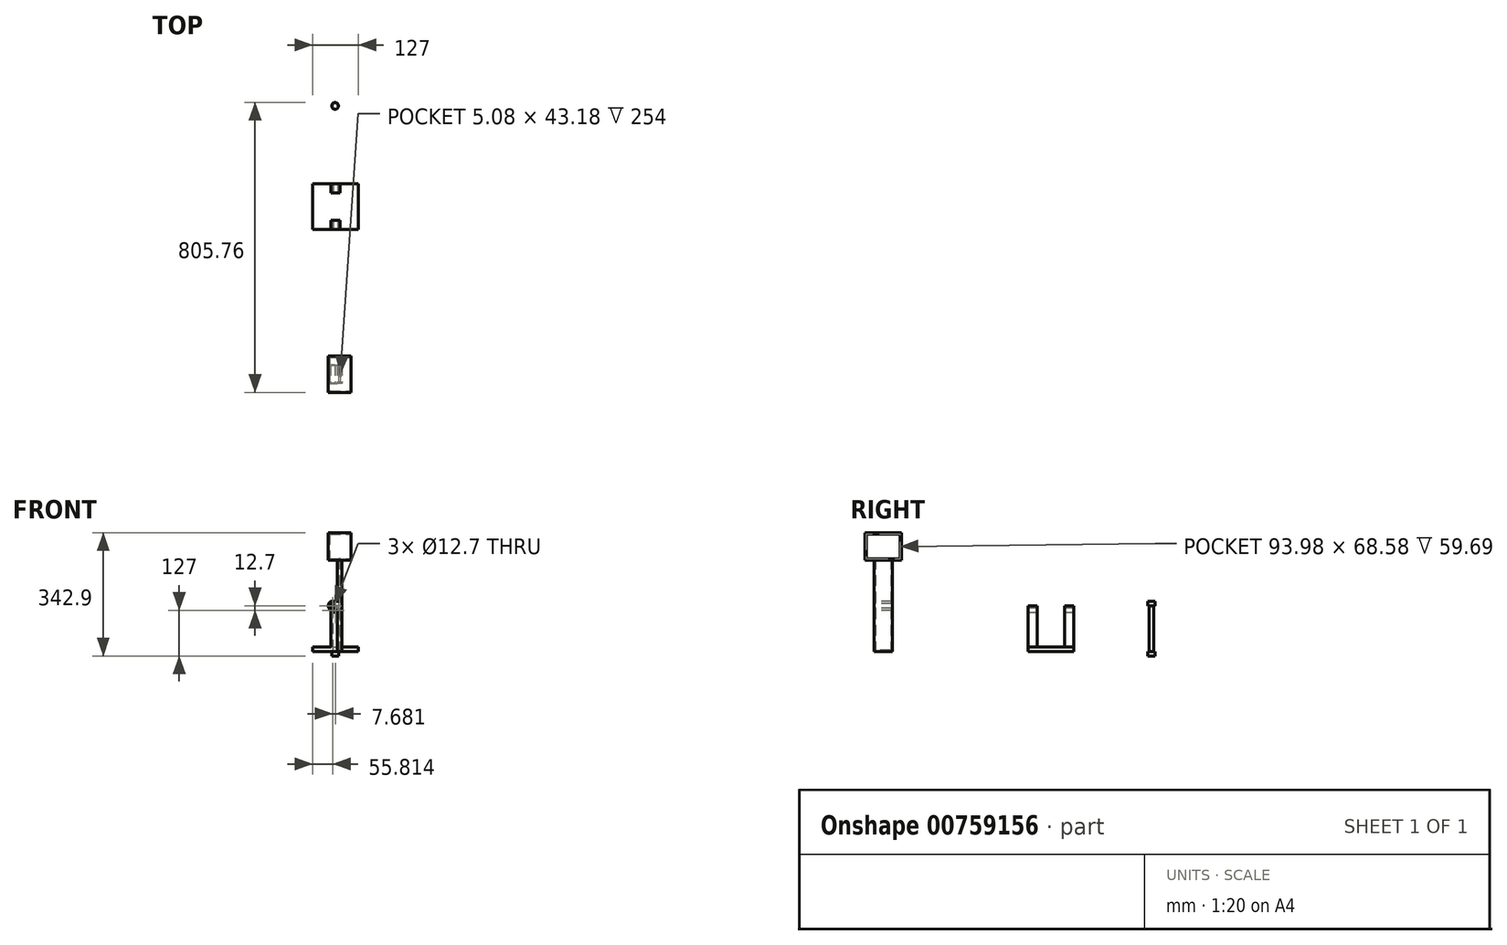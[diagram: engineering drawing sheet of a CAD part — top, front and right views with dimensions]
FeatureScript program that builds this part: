
annotation { "Feature Type Name" : "Feature", "Feature Type Description" : "" }
export const myFeature = defineFeature(function(context is Context, id is Id, definition is map)
    precondition{}
    {
        {
            var Q0;
            Q0=qCreatedBy(makeId("Top.planeOp"),FACE);
            var sketch = newSketch(context, id + "F0", { "sketchPlane" : qUnion([Q0])});
            skLineSegment(sketch, "E0.bottom", {"start": v(-62.3, 72.06) * mm, "end": v(64.7, 72.06) * mm});
            skLineSegment(sketch, "E0.top", {"start": v(-62.3, -54.94) * mm, "end": v(64.7, -54.94) * mm});
            skLineSegment(sketch, "E0.left", {"start": v(-62.3, 72.06) * mm, "end": v(-62.3, -54.94) * mm});
            skLineSegment(sketch, "E0.right", {"start": v(64.7, 72.06) * mm, "end": v(64.7, -54.94) * mm});
            skCircle(sketch, "E1", {"center": v(0, 288.32) * mm, "radius": 6.35 * mm});
            skLineSegment(sketch, "E2.bottom", {"start": v(18.92, -431.71) * mm, "end": v(6.22, -431.71) * mm});
            skLineSegment(sketch, "E2.top", {"start": v(18.92, -482.51) * mm, "end": v(6.22, -482.51) * mm});
            skLineSegment(sketch, "E2.left", {"start": v(18.92, -431.71) * mm, "end": v(18.92, -482.51) * mm});
            skLineSegment(sketch, "E2.right", {"start": v(6.22, -431.71) * mm, "end": v(6.22, -482.51) * mm});
            skPoint(sketch, "E2.middle", {"position": v(12.57, -457.11) * mm});
            skSolve(sketch);
        }
        {
            var Q0;
            Q0=makeQuery(id+"F0.imprint","IMPRINT",FACE,{"disambiguationData":[TD([[makeQuery(id+"F0.imprint","IMPRINT",EDGE,{"derivedFrom":sQuery(id+"F0.wireOp",EDGE,"E0.bottom")}),-1.0]])]});
            extrude(context, id + "F1", {"entities" : qUnion([Q0]), "depth" : 12.7 * mm, "offsetDistance" : 25.4 * mm});
        }
        {
            var Q0;
            Q0=makeQuery(id+"F1.opExtrude","CAP_FACE",FACE,{"disambiguationData":[OSD([sQuery(id+"F0.wireOp",EDGE,"E0.bottom"),sQuery(id+"F0.wireOp",EDGE,"E0.top"),sQuery(id+"F0.wireOp",EDGE,"E0.left"),sQuery(id+"F0.wireOp",EDGE,"E0.right")])],"isStart":false});
            var sketch = newSketch(context, id + "F2", { "sketchPlane" : qUnion([Q0])});
            skPoint(sketch, "E3.firstSnap0", {"position": v(1.2, 72.06) * mm});
            skLineSegment(sketch, "E4.bottom", {"start": v(13.9, -54.94) * mm, "end": v(-11.5, -54.94) * mm});
            skLineSegment(sketch, "E4.top", {"start": v(13.9, -29.54) * mm, "end": v(-11.5, -29.54) * mm});
            skLineSegment(sketch, "E4.left", {"start": v(13.9, -54.94) * mm, "end": v(13.9, -29.54) * mm});
            skLineSegment(sketch, "E4.right", {"start": v(-11.5, -54.94) * mm, "end": v(-11.5, -29.54) * mm});
            skPoint(sketch, "E4.middle", {"position": v(1.2, -42.24) * mm});
            skLineSegment(sketch, "E5.bottom", {"start": v(-11.5, 72.06) * mm, "end": v(13.9, 72.06) * mm});
            skLineSegment(sketch, "E5.top", {"start": v(-11.5, 46.66) * mm, "end": v(13.9, 46.66) * mm});
            skLineSegment(sketch, "E5.left", {"start": v(-11.5, 72.06) * mm, "end": v(-11.5, 46.66) * mm});
            skLineSegment(sketch, "E5.right", {"start": v(13.9, 72.06) * mm, "end": v(13.9, 46.66) * mm});
            skPoint(sketch, "E5.middle", {"position": v(1.2, 59.36) * mm});
            skPoint(sketch, "E5.middle.positionSnap0", {"position": v(1.2, -29.54) * mm});
            skPoint(sketch, "E5.centerSnap0", {"position": v(1.2, -29.54) * mm});
            skSolve(sketch);
        }
        {
            var Q0;
            Q0 = qSketchRegion(id + "F2", true);
            extrude(context, id + "F3", {"entities" : qUnion([Q0]), "operationType" : NewBodyOperationType.ADD, "depth" : 114.3 * mm, "offsetDistance" : 25.4 * mm});
        }
        {
            var Q0;
            Q0=makeQuery(id+"F3.opExtrude","CAP_EDGE",EDGE,{"disambiguationData":[OSD([sQuery(id+"F2.wireOp",EDGE,"E4.left")])],"isStart":false});
            fillet(context, id + "F4", {"entities" : qUnion([Q0]), "radius" : 12.7 * mm, "tangentPropagation" : true, "allowEdgeOverflow" : false});
        }
        {
            var Q0;
            Q0=makeQuery(id+"F3.opExtrude","CAP_EDGE",EDGE,{"disambiguationData":[OSD([sQuery(id+"F2.wireOp",EDGE,"E4.right")])],"isStart":false});
            fillet(context, id + "F5", {"entities" : qUnion([Q0]), "radius" : 12.7 * mm, "tangentPropagation" : true, "allowEdgeOverflow" : false});
        }
        {
            var Q0;
            Q0=makeQuery(id+"F3.opExtrude","CAP_EDGE",EDGE,{"disambiguationData":[OSD([sQuery(id+"F2.wireOp",EDGE,"E5.left")])],"isStart":false});
            var Q1;
            Q1=makeQuery(id+"F3.opExtrude","CAP_EDGE",EDGE,{"disambiguationData":[OSD([sQuery(id+"F2.wireOp",EDGE,"E5.right")])],"isStart":false});
            fillet(context, id + "F6", {"entities" : qUnion([Q0, Q1]), "radius" : 12.7 * mm, "tangentPropagation" : true, "allowEdgeOverflow" : false});
        }
        {
            var Q0;
            Q0=makeQuery(id+"F3.boolean.opBoolean","MERGE",FACE,{"derivedFrom":[makeQuery(id+"F1.opExtrude","SWEPT_FACE",FACE,{"disambiguationData":[OSD([sQuery(id+"F0.wireOp",EDGE,"E0.top")])]}),makeQuery(id+"F3.opExtrude","SWEPT_FACE",FACE,{"disambiguationData":[OSD([sQuery(id+"F2.wireOp",EDGE,"E4.bottom")])]})]});
            var sketch = newSketch(context, id + "F7", { "sketchPlane" : qUnion([Q0])});
            skCircle(sketch, "E6", {"center": v(1.2, 114.3) * mm, "radius": 6.35 * mm});
            skSolve(sketch);
        }
        {
            var Q0;
            Q0=makeQuery(id+"F7.imprint","IMPRINT",FACE,{"disambiguationData":[TD([[makeQuery(id+"F7.imprint","IMPRINT",EDGE,{"derivedFrom":sQuery(id+"F7.wireOp",EDGE,"E6")}),1.0]])]});
            extrude(context, id + "F8", {"entities" : qUnion([Q0]), "operationType" : NewBodyOperationType.REMOVE, "oppositeDirection" : true, "depth" : 153.42 * mm, "offsetDistance" : 25.4 * mm});
        }
        {
            var Q0;
            Q0=makeQuery(id+"F0.imprint","IMPRINT",FACE,{"disambiguationData":[TD([[makeQuery(id+"F0.imprint","IMPRINT",EDGE,{"derivedFrom":sQuery(id+"F0.wireOp",EDGE,"E1")}),1.0]])]});
            extrude(context, id + "F9", {"entities" : qUnion([Q0]), "depth" : 127 * mm, "offsetDistance" : 25.4 * mm});
        }
        {
            var Q0;
            Q0=makeQuery(id+"F9.opExtrude","CAP_FACE",FACE,{"disambiguationData":[OSD([sQuery(id+"F0.wireOp",EDGE,"E1")])],"isStart":false});
            var sketch = newSketch(context, id + "F10", { "sketchPlane" : qUnion([Q0])});
            skCircle(sketch, "E7", {"center": v(0, 288.32) * mm, "radius": 9.53 * mm});
            skSolve(sketch);
        }
        {
            var Q0;
            Q0 = qSketchRegion(id + "F10", true);
            extrude(context, id + "F11", {"entities" : qUnion([Q0]), "operationType" : NewBodyOperationType.ADD, "depth" : 12.7 * mm, "offsetDistance" : 25.4 * mm});
        }
        {
            var Q0;
            Q0=makeQuery(id+"F9.opExtrude","CAP_FACE",FACE,{"disambiguationData":[OSD([sQuery(id+"F0.wireOp",EDGE,"E1")])],"isStart":true});
            var sketch = newSketch(context, id + "F12", { "sketchPlane" : qUnion([Q0])});
            skCircle(sketch, "E8", {"center": v(0, -288.32) * mm, "radius": 9.53 * mm});
            skSolve(sketch);
        }
        {
            var Q0;
            Q0 = qSketchRegion(id + "F12", true);
            extrude(context, id + "F13", {"entities" : qUnion([Q0]), "operationType" : NewBodyOperationType.ADD, "depth" : 12.7 * mm, "offsetDistance" : 25.4 * mm});
        }
        {
            var Q0;
            Q0=makeQuery(id+"F0.imprint","IMPRINT",FACE,{"disambiguationData":[TD([[makeQuery(id+"F0.imprint","IMPRINT",EDGE,{"derivedFrom":sQuery(id+"F0.wireOp",EDGE,"E2.bottom")}),1.0]])]});
            extrude(context, id + "F14", {"entities" : qUnion([Q0]), "depth" : 254 * mm, "offsetDistance" : 25.4 * mm});
        }
        {
            var Q0;
            Q0=makeQuery(id+"F14.opExtrude","CAP_FACE",FACE,{"disambiguationData":[OSD([sQuery(id+"F0.wireOp",EDGE,"E2.bottom"),sQuery(id+"F0.wireOp",EDGE,"E2.top"),sQuery(id+"F0.wireOp",EDGE,"E2.left"),sQuery(id+"F0.wireOp",EDGE,"E2.right")])],"isStart":false});
            var sketch = newSketch(context, id + "F15", { "sketchPlane" : qUnion([Q0])});
            skLineSegment(sketch, "E9.bottom", {"start": v(-19.18, -406.31) * mm, "end": v(44.32, -406.31) * mm});
            skLineSegment(sketch, "E9.top", {"start": v(-19.18, -507.91) * mm, "end": v(44.32, -507.91) * mm});
            skLineSegment(sketch, "E9.left", {"start": v(-19.18, -406.31) * mm, "end": v(-19.18, -507.91) * mm});
            skLineSegment(sketch, "E9.right", {"start": v(44.32, -406.31) * mm, "end": v(44.32, -507.91) * mm});
            skPoint(sketch, "E9.middle", {"position": v(12.57, -457.11) * mm});
            skPoint(sketch, "E9.middle.positionSnap0", {"position": v(12.57, -431.71) * mm});
            skPoint(sketch, "E9.middle.positionSnap1", {"position": v(6.22, -457.11) * mm});
            skPoint(sketch, "E9.centerSnap0", {"position": v(12.57, -431.71) * mm});
            skPoint(sketch, "E9.centerSnap1", {"position": v(6.22, -457.11) * mm});
            skSolve(sketch);
        }
        {
            var Q0;
            Q0=makeQuery(id+"F15.imprint","IMPRINT",FACE,{"disambiguationData":[TD([[makeQuery(id+"F15.imprint","IMPRINT",EDGE,{"derivedFrom":makeQuery(id+"F14.opExtrude","CAP_EDGE",EDGE,{"disambiguationData":[OSD([sQuery(id+"F0.wireOp",EDGE,"E2.bottom")])],"isStart":false})}),1.0]])]});
            var Q1;
            Q1=makeQuery(id+"F15.imprint","IMPRINT",FACE,{"disambiguationData":[TD([[makeQuery(id+"F15.imprint","IMPRINT",EDGE,{"derivedFrom":sQuery(id+"F15.wireOp",EDGE,"E9.bottom")}),-1.0]])]});
            extrude(context, id + "F16", {"entities" : qUnion([Q0, Q1]), "operationType" : NewBodyOperationType.ADD, "depth" : 76.2 * mm, "offsetDistance" : 25.4 * mm});
        }
        {
            var Q0;
            Q0=makeQuery(id+"F16.opExtrude","SWEPT_FACE",FACE,{"disambiguationData":[OSD([sQuery(id+"F15.wireOp",EDGE,"E9.right")])]});
            shell(context, id + "F17", {"entities" : qUnion([Q0]), "thickness" : 3.8 * mm});
        }
        {
            var Q0;
            Q0=makeQuery(id+"F14.opExtrude","SWEPT_FACE",FACE,{"disambiguationData":[OSD([sQuery(id+"F0.wireOp",EDGE,"E2.right")])]});
            var sketch = newSketch(context, id + "F18", { "sketchPlane" : qUnion([Q0])});
            skPoint(sketch, "E10.middle", {"position": v(457.11, 127) * mm});
            skPoint(sketch, "E10.middle.positionSnap0", {"position": v(457.11, 0) * mm});
            skPoint(sketch, "E10.middle.positionSnap1", {"position": v(431.71, 127) * mm});
            skPoint(sketch, "E10.centerSnap0", {"position": v(457.11, 0) * mm});
            skPoint(sketch, "E10.centerSnap1", {"position": v(431.71, 127) * mm});
            skLineSegment(sketch, "E11.bottom", {"start": v(431.71, 139.7) * mm, "end": v(482.51, 139.7) * mm});
            skLineSegment(sketch, "E11.top", {"start": v(431.71, 114.3) * mm, "end": v(482.51, 114.3) * mm});
            skLineSegment(sketch, "E11.left", {"start": v(431.71, 139.7) * mm, "end": v(431.71, 114.3) * mm});
            skLineSegment(sketch, "E11.right", {"start": v(482.51, 139.7) * mm, "end": v(482.51, 114.3) * mm});
            skSolve(sketch);
        }
        {
            var Q0;
            Q0=makeQuery(id+"F18.imprint","IMPRINT",FACE,{"disambiguationData":[TD([[makeQuery(id+"F18.imprint","IMPRINT",EDGE,{"derivedFrom":sQuery(id+"F18.wireOp",EDGE,"E11.bottom")}),-1.0]])]});
            extrude(context, id + "F19", {"entities" : qUnion([Q0]), "operationType" : NewBodyOperationType.ADD, "depth" : 25.4 * mm, "offsetDistance" : 25.4 * mm});
        }
        {
            var Q0;
            Q0=makeQuery(id+"F19.opExtrude","CAP_EDGE",EDGE,{"disambiguationData":[OSD([sQuery(id+"F18.wireOp",EDGE,"E11.top")])],"isStart":false});
            var Q1;
            Q1=makeQuery(id+"F19.opExtrude","CAP_EDGE",EDGE,{"disambiguationData":[OSD([sQuery(id+"F18.wireOp",EDGE,"E11.bottom")])],"isStart":false});
            fillet(context, id + "F20", {"entities" : qUnion([Q0, Q1]), "radius" : 12.7 * mm, "tangentPropagation" : true, "allowEdgeOverflow" : false});
        }
        {
            var Q0;
            Q0=makeQuery(id+"F19.boolean.opBoolean","MERGE",FACE,{"derivedFrom":[makeQuery(id+"F14.opExtrude","SWEPT_FACE",FACE,{"disambiguationData":[OSD([sQuery(id+"F0.wireOp",EDGE,"E2.top")])]}),makeQuery(id+"F19.opExtrude","SWEPT_FACE",FACE,{"disambiguationData":[OSD([sQuery(id+"F18.wireOp",EDGE,"E11.right")])]})]});
            var sketch = newSketch(context, id + "F21", { "sketchPlane" : qUnion([Q0])});
            skCircle(sketch, "E12", {"center": v(-6.48, 127) * mm, "radius": 6.35 * mm});
            skSolve(sketch);
        }
        {
            var Q0;
            Q0=makeQuery(id+"F21.imprint","IMPRINT",FACE,{"disambiguationData":[TD([[makeQuery(id+"F21.imprint","IMPRINT",EDGE,{"derivedFrom":sQuery(id+"F21.wireOp",EDGE,"E12")}),1.0]])]});
            extrude(context, id + "F22", {"entities" : qUnion([Q0]), "operationType" : NewBodyOperationType.REMOVE, "oppositeDirection" : true, "depth" : 80 * mm, "offsetDistance" : 25.4 * mm});
        }
    });
